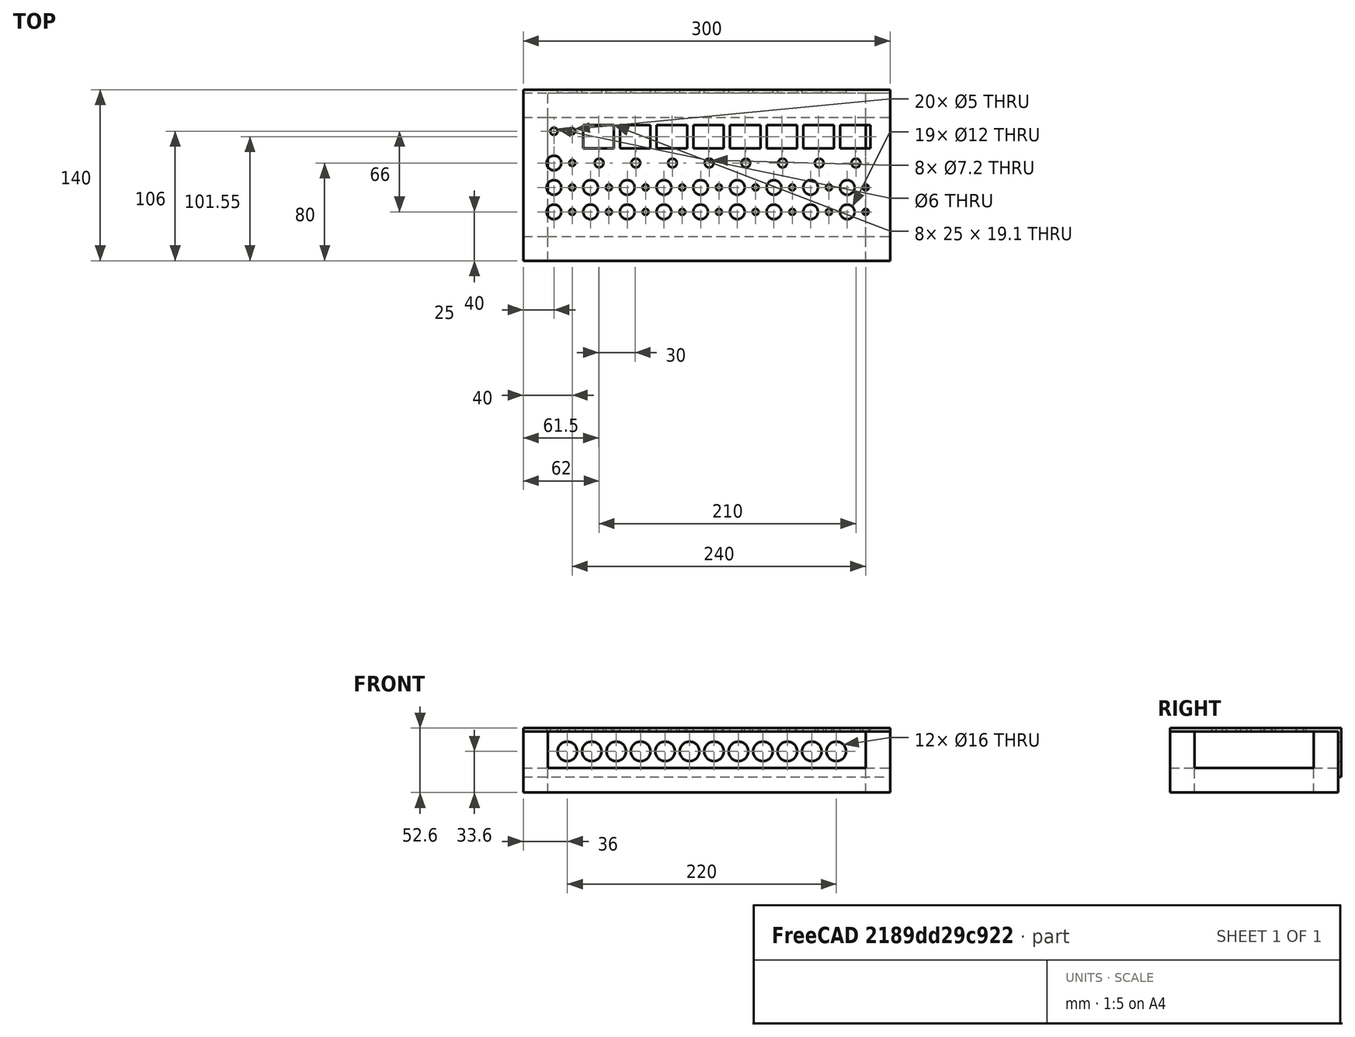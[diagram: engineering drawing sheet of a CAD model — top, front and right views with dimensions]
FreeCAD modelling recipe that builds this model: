
FCSTD DOCUMENT  (FreeCAD 1.0R38641 +678 (Git))
Label: astrobox_medium_krabice
License: All rights reserved
LicenseURL: https://en.wikipedia.org/wiki/All_rights_reserved
objects: Part::Cylinder×60, Part::Box×18, Part::MultiFuse×16, Part::Cut×2
note: 96 computed .brp shape members not serialized (recipe doc carries the construction recipe); baked Part::Feature solids carry a one-line shape summary decoded from their .brp

FEATURE [Part::Box] Box  label="Krychle"
  AttacherType = Attacher::AttachEngine3D
  Height = 40
  Length = 300
  Width = 140
FEATURE [Part::Box] Box001  label="Krychle001"
  AttacherType = Attacher::AttachEngine3D
  Height = 37.4
  Length = 300
  Width = 137.4
FEATURE [Part::Cut] Cut  label="horni kryt bez vrtani"
  Base = -> Box
  Refine = true
  Tool = -> Box001
FEATURE [Part::Cylinder] Cylinder  label="led 1"
  Angle = 360
  AttacherType = Attacher::AttachEngine3D
  FirstAngle = 0
  Height = 10
  Radius = 2.5
  SecondAngle = 0
FEATURE [Part::Cylinder] Cylinder019  label="tlacitko 1"
  Angle = 360
  AttacherType = Attacher::AttachEngine3D
  FirstAngle = 0
  Height = 10
  Placement = pos=(-15,0,0) rot=(0,0,1;0rad)
  Radius = 6
  SecondAngle = 0
FEATURE [Part::Box] Box002  label="7seg 1"
  AttacherType = Attacher::AttachEngine3D
  Height = 10
  Length = 25
  Placement = pos=(-21,52,0) rot=(0,0,1;0rad)
  Width = 19.1
FEATURE [Part::Cylinder] Cylinder038  label="pot 1"
  Angle = 360
  AttacherType = Attacher::AttachEngine3D
  FirstAngle = 0
  Height = 10
  Placement = pos=(-8,40,0) rot=(0,0,1;0rad)
  Radius = 3.6
  SecondAngle = 0
FEATURE [Part::Cylinder] Cylinder039  label="led 002"
  Angle = 360
  AttacherType = Attacher::AttachEngine3D
  FirstAngle = 0
  Height = 10
  Radius = 2.5
  SecondAngle = 0
FEATURE [Part::Cylinder] Cylinder040  label="tlacitko 002"
  Angle = 360
  AttacherType = Attacher::AttachEngine3D
  FirstAngle = 0
  Height = 10
  Placement = pos=(-15,0,0) rot=(0,0,1;0rad)
  Radius = 6
  SecondAngle = 0
FEATURE [Part::MultiFuse] Fusion  label="CTRL_5V"
  Refine = true
  Shapes = -> [Cylinder019,Cylinder]
FEATURE [Part::Cylinder] Cylinder041  label="led 003"
  Angle = 360
  AttacherType = Attacher::AttachEngine3D
  FirstAngle = 0
  Height = 10
  Radius = 2.5
  SecondAngle = 0
FEATURE [Part::Cylinder] Cylinder042  label="tlacitko 003"
  Angle = 360
  AttacherType = Attacher::AttachEngine3D
  FirstAngle = 0
  Height = 10
  Placement = pos=(-15,0,0) rot=(0,0,1;0rad)
  Radius = 6
  SecondAngle = 0
FEATURE [Part::MultiFuse] Fusion001  label="CTRL_6V"
  Placement = pos=(0,20,0) rot=(0,0,1;0rad)
  Refine = true
  Shapes = -> [Cylinder042,Cylinder041]
FEATURE [Part::Cylinder] Cylinder043  label="led 004"
  Angle = 360
  AttacherType = Attacher::AttachEngine3D
  FirstAngle = 0
  Height = 10
  Radius = 2.5
  SecondAngle = 0
FEATURE [Part::Cylinder] Cylinder044  label="tlacitko 004"
  Angle = 360
  AttacherType = Attacher::AttachEngine3D
  FirstAngle = 0
  Height = 10
  Placement = pos=(-15,0,0) rot=(0,0,1;0rad)
  Radius = 6
  SecondAngle = 0
FEATURE [Part::MultiFuse] Fusion002  label="CTRL_9V"
  Placement = pos=(0,40,0) rot=(0,0,1;0rad)
  Refine = true
  Shapes = -> [Cylinder044,Cylinder043]
FEATURE [Part::Cylinder] Cylinder045  label="tlacitko 005"
  Angle = 360
  AttacherType = Attacher::AttachEngine3D
  FirstAngle = 0
  Height = 10
  Placement = pos=(-15,20,0) rot=(0,0,1;0rad)
  Radius = 6
  SecondAngle = 0
FEATURE [Part::Cylinder] Cylinder046  label="led 005"
  Angle = 360
  AttacherType = Attacher::AttachEngine3D
  FirstAngle = 0
  Height = 10
  Placement = pos=(0,20,0) rot=(0,0,1;0rad)
  Radius = 2.5
  SecondAngle = 0
FEATURE [Part::MultiFuse] Fusion003  label="CTRL_12V 1"
  Placement = pos=(30,0,0) rot=(0,0,1;0rad)
  Refine = true
  Shapes = -> [Cylinder046,Cylinder045,Cylinder040,Cylinder039,Cylinder038,Box002]
FEATURE [Part::Box] Box003  label="7seg 002"
  AttacherType = Attacher::AttachEngine3D
  Height = 10
  Length = 25
  Placement = pos=(-21,52,0) rot=(0,0,1;0rad)
  Width = 19.1
FEATURE [Part::Cylinder] Cylinder047  label="pot 002"
  Angle = 360
  AttacherType = Attacher::AttachEngine3D
  FirstAngle = 0
  Height = 10
  Placement = pos=(-8,40,0) rot=(0,0,1;0rad)
  Radius = 3.6
  SecondAngle = 0
FEATURE [Part::Cylinder] Cylinder048  label="led 006"
  Angle = 360
  AttacherType = Attacher::AttachEngine3D
  FirstAngle = 0
  Height = 10
  Radius = 2.5
  SecondAngle = 0
FEATURE [Part::Cylinder] Cylinder049  label="tlacitko 006"
  Angle = 360
  AttacherType = Attacher::AttachEngine3D
  FirstAngle = 0
  Height = 10
  Placement = pos=(-15,0,0) rot=(0,0,1;0rad)
  Radius = 6
  SecondAngle = 0
FEATURE [Part::Cylinder] Cylinder050  label="tlacitko 007"
  Angle = 360
  AttacherType = Attacher::AttachEngine3D
  FirstAngle = 0
  Height = 10
  Placement = pos=(-15,20,0) rot=(0,0,1;0rad)
  Radius = 6
  SecondAngle = 0
FEATURE [Part::Cylinder] Cylinder051  label="led 007"
  Angle = 360
  AttacherType = Attacher::AttachEngine3D
  FirstAngle = 0
  Height = 10
  Placement = pos=(0,20,0) rot=(0,0,1;0rad)
  Radius = 2.5
  SecondAngle = 0
FEATURE [Part::MultiFuse] Fusion004  label="CTRL_12V 002"
  Placement = pos=(60,0,0) rot=(0,0,1;0rad)
  Refine = true
  Shapes = -> [Cylinder051,Cylinder050,Cylinder049,Cylinder048,Cylinder047,Box003]
FEATURE [Part::Box] Box004  label="7seg 003"
  AttacherType = Attacher::AttachEngine3D
  Height = 10
  Length = 25
  Placement = pos=(-21,52,0) rot=(0,0,1;0rad)
  Width = 19.1
FEATURE [Part::Cylinder] Cylinder052  label="pot 003"
  Angle = 360
  AttacherType = Attacher::AttachEngine3D
  FirstAngle = 0
  Height = 10
  Placement = pos=(-8,40,0) rot=(0,0,1;0rad)
  Radius = 3.6
  SecondAngle = 0
FEATURE [Part::Cylinder] Cylinder053  label="led 008"
  Angle = 360
  AttacherType = Attacher::AttachEngine3D
  FirstAngle = 0
  Height = 10
  Radius = 2.5
  SecondAngle = 0
FEATURE [Part::Cylinder] Cylinder054  label="tlacitko 008"
  Angle = 360
  AttacherType = Attacher::AttachEngine3D
  FirstAngle = 0
  Height = 10
  Placement = pos=(-15,0,0) rot=(0,0,1;0rad)
  Radius = 6
  SecondAngle = 0
FEATURE [Part::Cylinder] Cylinder055  label="tlacitko 009"
  Angle = 360
  AttacherType = Attacher::AttachEngine3D
  FirstAngle = 0
  Height = 10
  Placement = pos=(-15,20,0) rot=(0,0,1;0rad)
  Radius = 6
  SecondAngle = 0
FEATURE [Part::Cylinder] Cylinder056  label="led 009"
  Angle = 360
  AttacherType = Attacher::AttachEngine3D
  FirstAngle = 0
  Height = 10
  Placement = pos=(0,20,0) rot=(0,0,1;0rad)
  Radius = 2.5
  SecondAngle = 0
FEATURE [Part::MultiFuse] Fusion005  label="CTRL_12V 003"
  Placement = pos=(90,0,0) rot=(0,0,1;0rad)
  Refine = true
  Shapes = -> [Cylinder056,Cylinder055,Cylinder054,Cylinder053,Cylinder052,Box004]
FEATURE [Part::Box] Box005  label="7seg 004"
  AttacherType = Attacher::AttachEngine3D
  Height = 10
  Length = 25
  Placement = pos=(-21,52,0) rot=(0,0,1;0rad)
  Width = 19.1
FEATURE [Part::Cylinder] Cylinder057  label="pot 004"
  Angle = 360
  AttacherType = Attacher::AttachEngine3D
  FirstAngle = 0
  Height = 10
  Placement = pos=(-8,40,0) rot=(0,0,1;0rad)
  Radius = 3.6
  SecondAngle = 0
FEATURE [Part::Cylinder] Cylinder058  label="led 010"
  Angle = 360
  AttacherType = Attacher::AttachEngine3D
  FirstAngle = 0
  Height = 10
  Radius = 2.5
  SecondAngle = 0
FEATURE [Part::Cylinder] Cylinder059  label="tlacitko 010"
  Angle = 360
  AttacherType = Attacher::AttachEngine3D
  FirstAngle = 0
  Height = 10
  Placement = pos=(-15,0,0) rot=(0,0,1;0rad)
  Radius = 6
  SecondAngle = 0
FEATURE [Part::Cylinder] Cylinder060  label="tlacitko 011"
  Angle = 360
  AttacherType = Attacher::AttachEngine3D
  FirstAngle = 0
  Height = 10
  Placement = pos=(-15,20,0) rot=(0,0,1;0rad)
  Radius = 6
  SecondAngle = 0
FEATURE [Part::Cylinder] Cylinder061  label="led 011"
  Angle = 360
  AttacherType = Attacher::AttachEngine3D
  FirstAngle = 0
  Height = 10
  Placement = pos=(0,20,0) rot=(0,0,1;0rad)
  Radius = 2.5
  SecondAngle = 0
FEATURE [Part::MultiFuse] Fusion006  label="CTRL_12V 004"
  Placement = pos=(120,0,0) rot=(0,0,1;0rad)
  Refine = true
  Shapes = -> [Cylinder061,Cylinder060,Cylinder059,Cylinder058,Cylinder057,Box005]
FEATURE [Part::Box] Box006  label="7seg 005"
  AttacherType = Attacher::AttachEngine3D
  Height = 10
  Length = 25
  Placement = pos=(-21,52,0) rot=(0,0,1;0rad)
  Width = 19.1
FEATURE [Part::Cylinder] Cylinder062  label="pot 005"
  Angle = 360
  AttacherType = Attacher::AttachEngine3D
  FirstAngle = 0
  Height = 10
  Placement = pos=(-8,40,0) rot=(0,0,1;0rad)
  Radius = 3.6
  SecondAngle = 0
FEATURE [Part::Cylinder] Cylinder063  label="led 012"
  Angle = 360
  AttacherType = Attacher::AttachEngine3D
  FirstAngle = 0
  Height = 10
  Radius = 2.5
  SecondAngle = 0
FEATURE [Part::Cylinder] Cylinder064  label="tlacitko 012"
  Angle = 360
  AttacherType = Attacher::AttachEngine3D
  FirstAngle = 0
  Height = 10
  Placement = pos=(-15,0,0) rot=(0,0,1;0rad)
  Radius = 6
  SecondAngle = 0
FEATURE [Part::Cylinder] Cylinder065  label="tlacitko 013"
  Angle = 360
  AttacherType = Attacher::AttachEngine3D
  FirstAngle = 0
  Height = 10
  Placement = pos=(-15,20,0) rot=(0,0,1;0rad)
  Radius = 6
  SecondAngle = 0
FEATURE [Part::Cylinder] Cylinder066  label="led 013"
  Angle = 360
  AttacherType = Attacher::AttachEngine3D
  FirstAngle = 0
  Height = 10
  Placement = pos=(0,20,0) rot=(0,0,1;0rad)
  Radius = 2.5
  SecondAngle = 0
FEATURE [Part::MultiFuse] Fusion007  label="CTRL_12V 005"
  Placement = pos=(150,0,0) rot=(0,0,1;0rad)
  Refine = true
  Shapes = -> [Cylinder066,Cylinder065,Cylinder064,Cylinder063,Cylinder062,Box006]
FEATURE [Part::Box] Box007  label="7seg 006"
  AttacherType = Attacher::AttachEngine3D
  Height = 10
  Length = 25
  Placement = pos=(-21,52,0) rot=(0,0,1;0rad)
  Width = 19.1
FEATURE [Part::Cylinder] Cylinder067  label="pot 006"
  Angle = 360
  AttacherType = Attacher::AttachEngine3D
  FirstAngle = 0
  Height = 10
  Placement = pos=(-8,40,0) rot=(0,0,1;0rad)
  Radius = 3.6
  SecondAngle = 0
FEATURE [Part::Cylinder] Cylinder068  label="led 014"
  Angle = 360
  AttacherType = Attacher::AttachEngine3D
  FirstAngle = 0
  Height = 10
  Radius = 2.5
  SecondAngle = 0
FEATURE [Part::Cylinder] Cylinder069  label="tlacitko 014"
  Angle = 360
  AttacherType = Attacher::AttachEngine3D
  FirstAngle = 0
  Height = 10
  Placement = pos=(-15,0,0) rot=(0,0,1;0rad)
  Radius = 6
  SecondAngle = 0
FEATURE [Part::Cylinder] Cylinder070  label="tlacitko 015"
  Angle = 360
  AttacherType = Attacher::AttachEngine3D
  FirstAngle = 0
  Height = 10
  Placement = pos=(-15,20,0) rot=(0,0,1;0rad)
  Radius = 6
  SecondAngle = 0
FEATURE [Part::Cylinder] Cylinder071  label="led 015"
  Angle = 360
  AttacherType = Attacher::AttachEngine3D
  FirstAngle = 0
  Height = 10
  Placement = pos=(0,20,0) rot=(0,0,1;0rad)
  Radius = 2.5
  SecondAngle = 0
FEATURE [Part::MultiFuse] Fusion008  label="CTRL_12V 006"
  Placement = pos=(180,0,0) rot=(0,0,1;0rad)
  Refine = true
  Shapes = -> [Cylinder071,Cylinder070,Cylinder069,Cylinder068,Cylinder067,Box007]
FEATURE [Part::Box] Box008  label="7seg 007"
  AttacherType = Attacher::AttachEngine3D
  Height = 10
  Length = 25
  Placement = pos=(-21,52,0) rot=(0,0,1;0rad)
  Width = 19.1
FEATURE [Part::Cylinder] Cylinder072  label="pot 007"
  Angle = 360
  AttacherType = Attacher::AttachEngine3D
  FirstAngle = 0
  Height = 10
  Placement = pos=(-8,40,0) rot=(0,0,1;0rad)
  Radius = 3.6
  SecondAngle = 0
FEATURE [Part::Cylinder] Cylinder073  label="led 016"
  Angle = 360
  AttacherType = Attacher::AttachEngine3D
  FirstAngle = 0
  Height = 10
  Radius = 2.5
  SecondAngle = 0
FEATURE [Part::Cylinder] Cylinder074  label="tlacitko 016"
  Angle = 360
  AttacherType = Attacher::AttachEngine3D
  FirstAngle = 0
  Height = 10
  Placement = pos=(-15,0,0) rot=(0,0,1;0rad)
  Radius = 6
  SecondAngle = 0
FEATURE [Part::Cylinder] Cylinder075  label="tlacitko 017"
  Angle = 360
  AttacherType = Attacher::AttachEngine3D
  FirstAngle = 0
  Height = 10
  Placement = pos=(-15,20,0) rot=(0,0,1;0rad)
  Radius = 6
  SecondAngle = 0
FEATURE [Part::Cylinder] Cylinder076  label="led 017"
  Angle = 360
  AttacherType = Attacher::AttachEngine3D
  FirstAngle = 0
  Height = 10
  Placement = pos=(0,20,0) rot=(0,0,1;0rad)
  Radius = 2.5
  SecondAngle = 0
FEATURE [Part::MultiFuse] Fusion009  label="CTRL_12V 007"
  Placement = pos=(210,0,0) rot=(0,0,1;0rad)
  Refine = true
  Shapes = -> [Cylinder076,Cylinder075,Cylinder074,Cylinder073,Cylinder072,Box008]
FEATURE [Part::Box] Box009  label="7seg 008"
  AttacherType = Attacher::AttachEngine3D
  Height = 10
  Length = 25
  Placement = pos=(-21,52,0) rot=(0,0,1;0rad)
  Width = 19.1
FEATURE [Part::Cylinder] Cylinder077  label="pot 008"
  Angle = 360
  AttacherType = Attacher::AttachEngine3D
  FirstAngle = 0
  Height = 10
  Placement = pos=(-8,40,0) rot=(0,0,1;0rad)
  Radius = 3.6
  SecondAngle = 0
FEATURE [Part::Cylinder] Cylinder078  label="led 018"
  Angle = 360
  AttacherType = Attacher::AttachEngine3D
  FirstAngle = 0
  Height = 10
  Radius = 2.5
  SecondAngle = 0
FEATURE [Part::Cylinder] Cylinder079  label="tlacitko 018"
  Angle = 360
  AttacherType = Attacher::AttachEngine3D
  FirstAngle = 0
  Height = 10
  Placement = pos=(-15,0,0) rot=(0,0,1;0rad)
  Radius = 6
  SecondAngle = 0
FEATURE [Part::Cylinder] Cylinder080  label="tlacitko 019"
  Angle = 360
  AttacherType = Attacher::AttachEngine3D
  FirstAngle = 0
  Height = 10
  Placement = pos=(-15,20,0) rot=(0,0,1;0rad)
  Radius = 6
  SecondAngle = 0
FEATURE [Part::Cylinder] Cylinder081  label="led 019"
  Angle = 360
  AttacherType = Attacher::AttachEngine3D
  FirstAngle = 0
  Height = 10
  Placement = pos=(0,20,0) rot=(0,0,1;0rad)
  Radius = 2.5
  SecondAngle = 0
FEATURE [Part::MultiFuse] Fusion010  label="CTRL_12V 008"
  Placement = pos=(240,0,0) rot=(0,0,1;0rad)
  Refine = true
  Shapes = -> [Cylinder081,Cylinder080,Cylinder079,Cylinder078,Cylinder077,Box009]
FEATURE [Part::MultiFuse] Fusion011  label="CTRL"
  Placement = pos=(40,40,35) rot=(0,0,1;0rad)
  Refine = true
  Shapes = -> [Fusion,Fusion001,Fusion002,Fusion003,Fusion004,Fusion005,Fusion006,Fusion007,Fusion008,Fusion009,Fusion010]
FEATURE [Part::Box] Box010  label="kostra leva zadni"
  AttacherType = Attacher::AttachEngine3D
  Height = 50
  Length = 20
  Placement = pos=(0,117.4,-12.6) rot=(0,0,1;0rad)
  Width = 20
FEATURE [Part::Box] Box011  label="kostra prava zadni"
  AttacherType = Attacher::AttachEngine3D
  Height = 50
  Length = 20
  Placement = pos=(280,117.4,-12.6) rot=(0,0,1;0rad)
  Width = 20
FEATURE [Part::Box] Box012  label="kostra leva predni"
  AttacherType = Attacher::AttachEngine3D
  Height = 50
  Length = 20
  Placement = pos=(0,0,-12.6) rot=(0,0,1;0rad)
  Width = 20
FEATURE [Part::Box] Box013  label="kostra prava predni"
  AttacherType = Attacher::AttachEngine3D
  Height = 50
  Length = 20
  Placement = pos=(280,0,-12.6) rot=(0,0,1;0rad)
  Width = 20
FEATURE [Part::Box] Box014  label="kostra predni dolni"
  AttacherType = Attacher::AttachEngine3D
  Height = 20
  Length = 260
  Placement = pos=(20,0,-12.6) rot=(0,0,1;0rad)
  Width = 20
FEATURE [Part::Box] Box015  label="kostra zadni dolni"
  AttacherType = Attacher::AttachEngine3D
  Height = 20
  Length = 260
  Placement = pos=(20,117.4,-12.6) rot=(0,0,1;0rad)
  Width = 20
FEATURE [Part::Box] Box016  label="kostra leva dolni"
  AttacherType = Attacher::AttachEngine3D
  Height = 20
  Length = 20
  Placement = pos=(0,20,-12.6) rot=(0,0,1;0rad)
  Width = 97.4
FEATURE [Part::Box] Box017  label="kostra prava dolni"
  AttacherType = Attacher::AttachEngine3D
  Height = 20
  Length = 20
  Placement = pos=(280,20,-12.6) rot=(0,0,1;0rad)
  Width = 97.4
FEATURE [Part::Cylinder] Cylinder082  label="konn in"
  Angle = 360
  AttacherType = Attacher::AttachEngine3D
  FirstAngle = 0
  Height = 10
  Placement = pos=(33,145,21) rot=(1,0,0;1.5708rad)
  Radius = 8
  SecondAngle = 0
FEATURE [Part::Cylinder] Cylinder083  label="konn out 5v"
  Angle = 360
  AttacherType = Attacher::AttachEngine3D
  FirstAngle = 0
  Height = 10
  Placement = pos=(53,145,21) rot=(1,0,0;1.5708rad)
  Radius = 8
  SecondAngle = 0
FEATURE [Part::Cylinder] Cylinder084  label="konn out 6v"
  Angle = 360
  AttacherType = Attacher::AttachEngine3D
  FirstAngle = 0
  Height = 10
  Placement = pos=(73,145,21) rot=(1,0,0;1.5708rad)
  Radius = 8
  SecondAngle = 0
FEATURE [Part::Cylinder] Cylinder085  label="konn out 9v"
  Angle = 360
  AttacherType = Attacher::AttachEngine3D
  FirstAngle = 0
  Height = 10
  Placement = pos=(93,145,21) rot=(1,0,0;1.5708rad)
  Radius = 8
  SecondAngle = 0
FEATURE [Part::Cylinder] Cylinder086  label="konn out 12v 1"
  Angle = 360
  AttacherType = Attacher::AttachEngine3D
  FirstAngle = 0
  Height = 10
  Placement = pos=(113,145,21) rot=(1,0,0;1.5708rad)
  Radius = 8
  SecondAngle = 0
FEATURE [Part::Cylinder] Cylinder087  label="konn out 12v 002"
  Angle = 360
  AttacherType = Attacher::AttachEngine3D
  FirstAngle = 0
  Height = 10
  Placement = pos=(133,145,21) rot=(1,0,0;1.5708rad)
  Radius = 8
  SecondAngle = 0
FEATURE [Part::Cylinder] Cylinder088  label="konn out 12v 003"
  Angle = 360
  AttacherType = Attacher::AttachEngine3D
  FirstAngle = 0
  Height = 10
  Placement = pos=(153,145,21) rot=(1,0,0;1.5708rad)
  Radius = 8
  SecondAngle = 0
FEATURE [Part::Cylinder] Cylinder089  label="konn out 12v 004"
  Angle = 360
  AttacherType = Attacher::AttachEngine3D
  FirstAngle = 0
  Height = 10
  Placement = pos=(173,145,21) rot=(1,0,0;1.5708rad)
  Radius = 8
  SecondAngle = 0
FEATURE [Part::Cylinder] Cylinder090  label="konn out 12v 005"
  Angle = 360
  AttacherType = Attacher::AttachEngine3D
  FirstAngle = 0
  Height = 10
  Placement = pos=(193,145,21) rot=(1,0,0;1.5708rad)
  Radius = 8
  SecondAngle = 0
FEATURE [Part::Cylinder] Cylinder091  label="konn out 12v 006"
  Angle = 360
  AttacherType = Attacher::AttachEngine3D
  FirstAngle = 0
  Height = 10
  Placement = pos=(213,145,21) rot=(1,0,0;1.5708rad)
  Radius = 8
  SecondAngle = 0
FEATURE [Part::Cylinder] Cylinder092  label="konn out 12v 007"
  Angle = 360
  AttacherType = Attacher::AttachEngine3D
  FirstAngle = 0
  Height = 10
  Placement = pos=(233,145,21) rot=(1,0,0;1.5708rad)
  Radius = 8
  SecondAngle = 0
FEATURE [Part::Cylinder] Cylinder093  label="konn out 12v 008"
  Angle = 360
  AttacherType = Attacher::AttachEngine3D
  FirstAngle = 0
  Height = 10
  Placement = pos=(253,145,21) rot=(1,0,0;1.5708rad)
  Radius = 8
  SecondAngle = 0
FEATURE [Part::MultiFuse] Fusion012  label="konns"
  Placement = pos=(3,0,0) rot=(0,0,1;0rad)
  Refine = true
  Shapes = -> [Cylinder082,Cylinder083,Cylinder084,Cylinder085,Cylinder086,Cylinder087,Cylinder088,Cylinder089,Cylinder090,Cylinder091,Cylinder092,Cylinder093]
FEATURE [Part::Cylinder] Cylinder094  label="led 020"
  Angle = 360
  AttacherType = Attacher::AttachEngine3D
  FirstAngle = 0
  Height = 10
  Radius = 2.5
  SecondAngle = 0
FEATURE [Part::Cylinder] Cylinder095  label="tlacitko 020"
  Angle = 360
  AttacherType = Attacher::AttachEngine3D
  FirstAngle = 0
  Height = 10
  Placement = pos=(-15,0,0) rot=(0,0,1;0rad)
  Radius = 3
  SecondAngle = 0
FEATURE [Part::MultiFuse] Fusion013  label="POWER_ON"
  Placement = pos=(40,106,35) rot=(0,0,1;0rad)
  Refine = true
  Shapes = -> [Cylinder095,Cylinder094]
FEATURE [Part::MultiFuse] Fusion014
  Refine = true
  Shapes = -> [Fusion011,Fusion012,Fusion013]
FEATURE [Part::MultiFuse] Fusion015  label="kostra"
  Refine = true
  Shapes = -> [Box010,Box011,Box012,Box013,Box014,Box015,Box016,Box017]
FEATURE [Part::Cut] Cut001  label="horni kryt"
  Base = -> Cut
  Refine = true
  Tool = -> Fusion014
